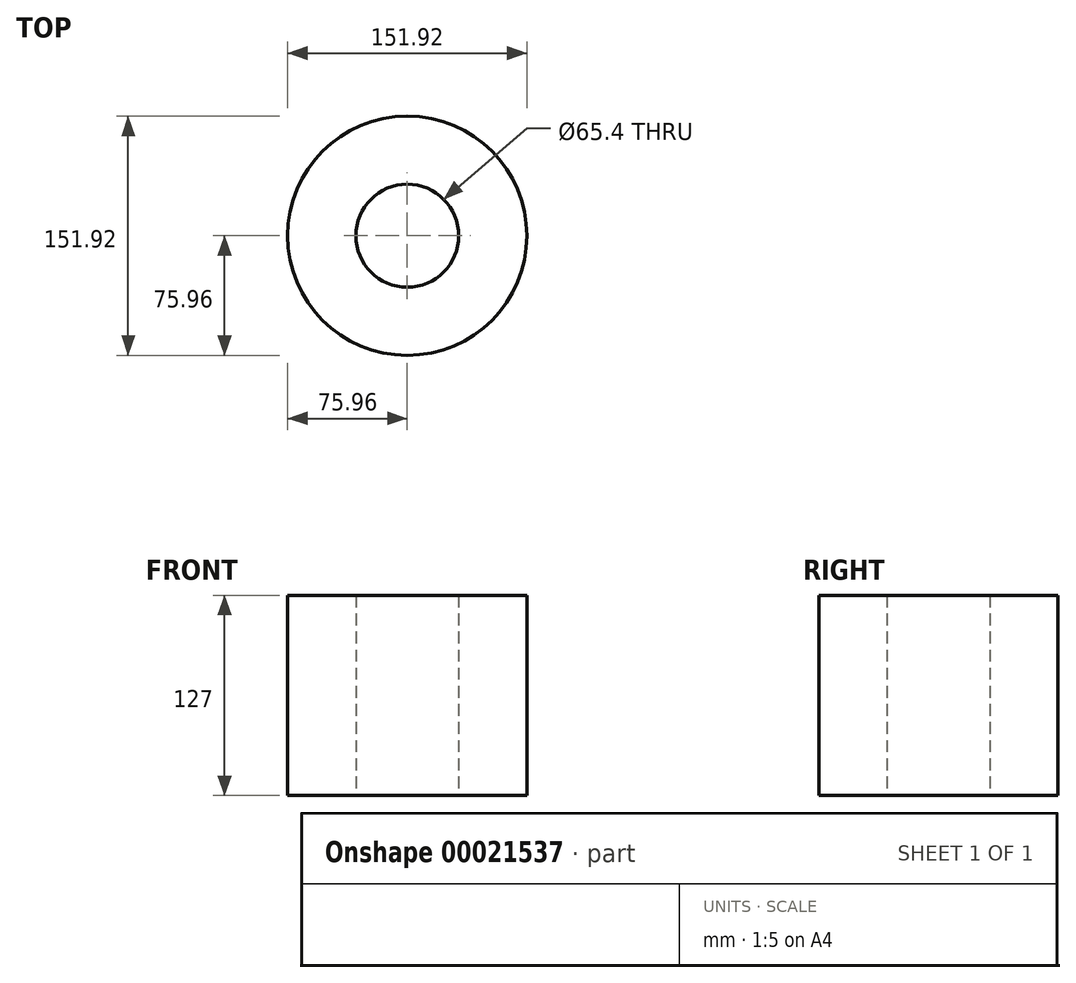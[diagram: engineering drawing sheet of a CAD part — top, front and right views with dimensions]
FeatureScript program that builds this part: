
annotation { "Feature Type Name" : "Feature", "Feature Type Description" : "" }
export const myFeature = defineFeature(function(context is Context, id is Id, definition is map)
    precondition{}
    {
        {
            var Q0;
            Q0=qCreatedBy(makeId("Top.planeOp"),FACE);
            var sketch = newSketch(context, id + "F0", { "sketchPlane" : qUnion([Q0])});
            skCircle(sketch, "E0", {"center": v(0, 0) * mm, "radius": 75.96 * mm});
            skCircle(sketch, "E1", {"center": v(0, 0) * mm, "radius": 32.7 * mm});
            skSolve(sketch);
        }
        {
            var Q0;
            Q0=makeQuery(id+"F0.imprint","IMPRINT",FACE,{"disambiguationData":[TD([[makeQuery(id+"F0.imprint","IMPRINT",EDGE,{"derivedFrom":sQuery(id+"F0.wireOp",EDGE,"E0")}),1.0]])]});
            extrude(context, id + "F1", {"entities" : qUnion([Q0]), "depth" : 63.5 * mm});
        }
        {
            var Q0;
            Q0=makeQuery(id+"F1.opExtrude","CAP_FACE",FACE,{"disambiguationData":[OSD([sQuery(id+"F0.wireOp",EDGE,"E0")])],"isStart":true});
            var Q1;
            Q1 = qSketchRegion(id + "F0", true);
            extrude(context, id + "F2", {"entities" : qUnion([Q0, Q1]), "operationType" : NewBodyOperationType.ADD, "depth" : 63.5 * mm});
        }
    });
